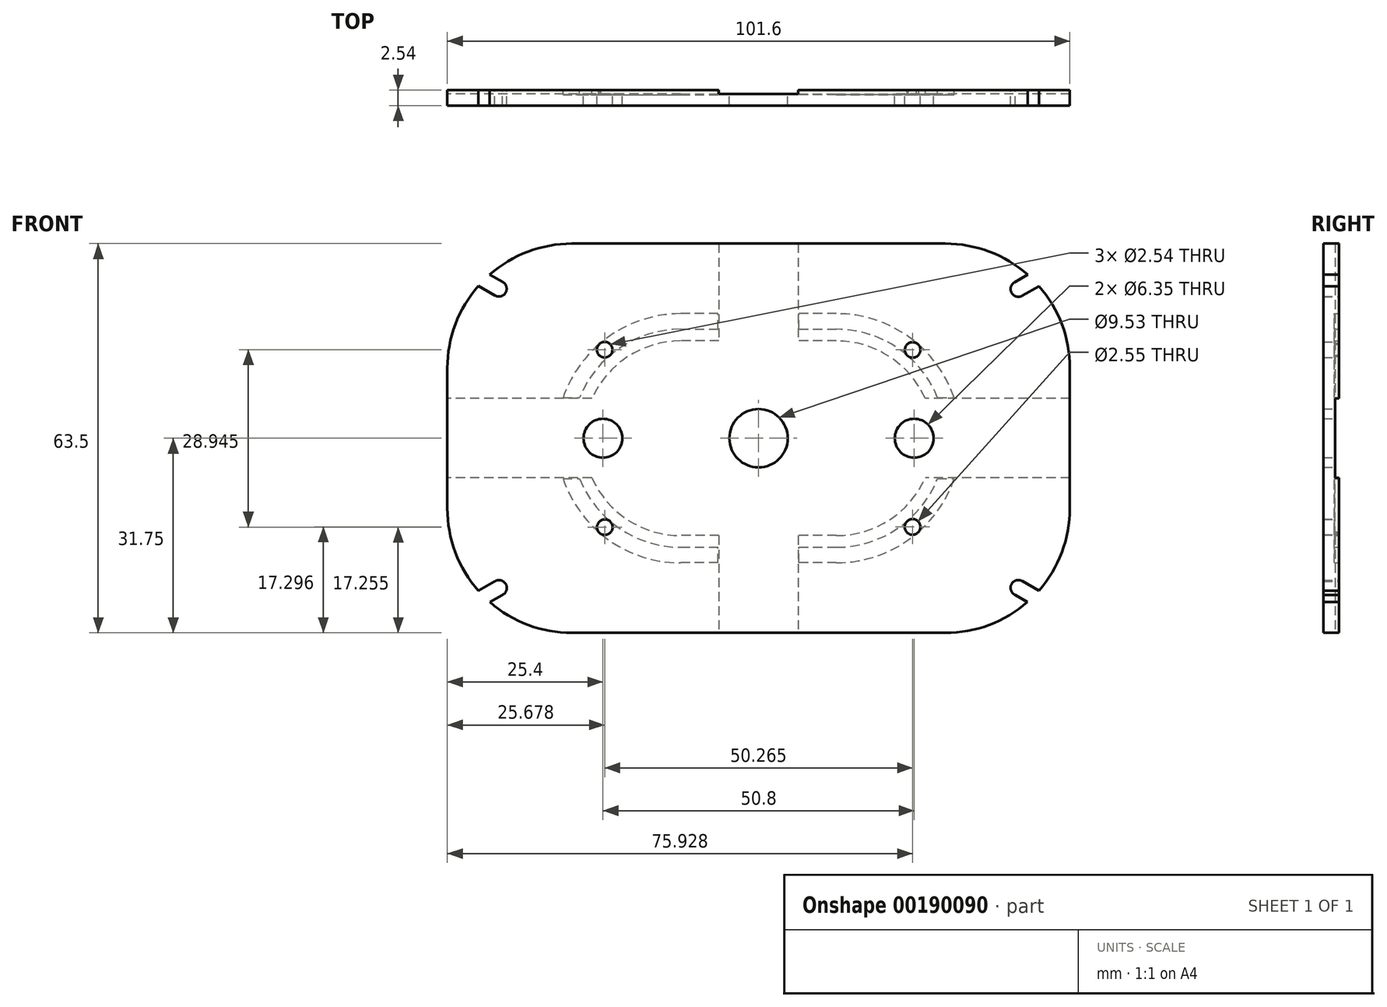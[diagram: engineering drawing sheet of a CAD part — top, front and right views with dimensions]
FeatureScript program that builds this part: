
annotation { "Feature Type Name" : "Feature", "Feature Type Description" : "" }
export const myFeature = defineFeature(function(context is Context, id is Id, definition is map)
    precondition{}
    {
        {
            var Q0;
            Q0=qCreatedBy(makeId("Front.planeOp"),FACE);
            var sketch = newSketch(context, id + "F0", { "sketchPlane" : qUnion([Q0])});
            skPoint(sketch, "E0.middle", {"position": v(0, 0) * mm});
            skLineSegment(sketch, "E1.bottom", {"start": v(-30.48, 31.75) * mm, "end": v(30.48, 31.75) * mm});
            skLineSegment(sketch, "E1.top", {"start": v(-30.48, -31.75) * mm, "end": v(30.48, -31.75) * mm});
            skLineSegment(sketch, "E1.left", {"start": v(-50.8, 11.43) * mm, "end": v(-50.8, -11.43) * mm});
            skLineSegment(sketch, "E1.right", {"start": v(50.8, 11.43) * mm, "end": v(50.8, -11.43) * mm});
            skPoint(sketch, "E2.visualSharp", {"position": v(-50.8, 31.75) * mm});
            skArc(sketch, "E2.filletArc", {"start": v(-30.48, 31.75) * mm, "mid": v(-44.85, 25.8) * mm, "end": v(-50.8, 11.43) * mm});
            skPoint(sketch, "E3.visualSharp", {"position": v(-50.8, -31.75) * mm});
            skArc(sketch, "E3.filletArc", {"start": v(-50.8, -11.43) * mm, "mid": v(-44.85, -25.8) * mm, "end": v(-30.48, -31.75) * mm});
            skPoint(sketch, "E4.visualSharp", {"position": v(50.8, -31.75) * mm});
            skArc(sketch, "E4.filletArc", {"start": v(30.48, -31.75) * mm, "mid": v(44.85, -25.8) * mm, "end": v(50.8, -11.43) * mm});
            skPoint(sketch, "E5.visualSharp", {"position": v(50.8, 31.75) * mm});
            skArc(sketch, "E5.filletArc", {"start": v(50.8, 11.43) * mm, "mid": v(44.85, 25.8) * mm, "end": v(30.48, 31.75) * mm});
            skSolve(sketch);
        }
        {
            var Q0;
            Q0 = qSketchRegion(id + "F0", true);
            extrude(context, id + "F1", {"entities" : qUnion([Q0]), "depth" : 2.54 * mm});
        }
        {
            var Q0;
            Q0=qCreatedBy(makeId("Front.planeOp"),FACE);
            var sketch = newSketch(context, id + "F2", { "sketchPlane" : qUnion([Q0])});
            skLineSegment(sketch, "E6.bottom", {"start": v(-12.7, 17.78) * mm, "end": v(12.7, 17.78) * mm});
            skLineSegment(sketch, "E6.top", {"start": v(-12.7, -17.78) * mm, "end": v(12.7, -17.78) * mm});
            skLineSegment(sketch, "E6.left", {"start": v(-30.48, 0) * mm, "end": v(-30.48, 0) * mm});
            skLineSegment(sketch, "E6.right", {"start": v(30.48, 0) * mm, "end": v(30.48, 0) * mm});
            skPoint(sketch, "E6.middle", {"position": v(0, 0) * mm});
            skPoint(sketch, "E7.visualSharp", {"position": v(-30.48, 17.78) * mm});
            skArc(sketch, "E7.filletArc", {"start": v(-12.7, 17.78) * mm, "mid": v(-25.27, 12.57) * mm, "end": v(-30.48, 0) * mm});
            skPoint(sketch, "E8.visualSharp", {"position": v(-30.48, -17.78) * mm});
            skArc(sketch, "E8.filletArc", {"start": v(-30.48, 0) * mm, "mid": v(-25.27, -12.57) * mm, "end": v(-12.7, -17.78) * mm});
            skPoint(sketch, "E9.visualSharp", {"position": v(30.48, 17.78) * mm});
            skArc(sketch, "E9.filletArc", {"start": v(30.48, 0) * mm, "mid": v(25.27, 12.57) * mm, "end": v(12.7, 17.78) * mm});
            skPoint(sketch, "E10.visualSharp", {"position": v(30.48, -17.78) * mm});
            skArc(sketch, "E10.filletArc", {"start": v(12.7, -17.78) * mm, "mid": v(25.27, -12.57) * mm, "end": v(30.48, 0) * mm});
            skLineSegment(sketch, "E11.bottom", {"start": v(12.7, 20.32) * mm, "end": v(-12.7, 20.32) * mm});
            skLineSegment(sketch, "E11.top", {"start": v(12.7, -20.32) * mm, "end": v(-12.7, -20.32) * mm});
            skLineSegment(sketch, "E11.left", {"start": v(33.02, 0) * mm, "end": v(33.02, 0) * mm});
            skLineSegment(sketch, "E11.right", {"start": v(-33.02, 0) * mm, "end": v(-33.02, 0) * mm});
            skPoint(sketch, "E12.visualSharp", {"position": v(-33.02, 20.32) * mm});
            skArc(sketch, "E12.filletArc", {"start": v(-12.7, 20.32) * mm, "mid": v(-27.07, 14.37) * mm, "end": v(-33.02, 0) * mm});
            skPoint(sketch, "E13.visualSharp", {"position": v(-33.02, -20.32) * mm});
            skArc(sketch, "E13.filletArc", {"start": v(-33.02, 0) * mm, "mid": v(-27.07, -14.37) * mm, "end": v(-12.7, -20.32) * mm});
            skPoint(sketch, "E14.visualSharp", {"position": v(33.02, -20.32) * mm});
            skArc(sketch, "E14.filletArc", {"start": v(12.7, -20.32) * mm, "mid": v(27.07, -14.37) * mm, "end": v(33.02, 0) * mm});
            skPoint(sketch, "E15.visualSharp", {"position": v(33.02, 20.32) * mm});
            skArc(sketch, "E15.filletArc", {"start": v(33.02, 0) * mm, "mid": v(27.07, 14.37) * mm, "end": v(12.7, 20.32) * mm});
            skSolve(sketch);
        }
        {
            var Q0;
            Q0 = qSketchRegion(id + "F2", true);
            extrude(context, id + "F3", {"entities" : qUnion([Q0]), "operationType" : NewBodyOperationType.ADD, "oppositeDirection" : true, "depth" : 12.7 * mm});
        }
        {
            var Q0;
            Q0=makeQuery(id+"F3.opExtrude","SWEPT_FACE",FACE,{"disambiguationData":[OSD([sQuery(id+"F2.wireOp",EDGE,"E11.bottom")])]});
            var sketch = newSketch(context, id + "F4", { "sketchPlane" : qUnion([Q0])});
            skLineSegment(sketch, "E16", {"start": v(0, 12.7) * mm, "end": v(-6.6, 12.7) * mm});
            skLineSegment(sketch, "E17", {"start": v(-6.6, 12.7) * mm, "end": v(-6.6, 0) * mm});
            skLineSegment(sketch, "E18", {"start": v(-6.6, 0) * mm, "end": v(6.6, 0) * mm});
            skLineSegment(sketch, "E19", {"start": v(6.6, 0) * mm, "end": v(6.6, 12.7) * mm});
            skLineSegment(sketch, "E20", {"start": v(6.6, 12.7) * mm, "end": v(0, 12.7) * mm});
            skSolve(sketch);
        }
        {
            var Q0;
            Q0 = qSketchRegion(id + "F4", true);
            extrude(context, id + "F5", {"entities" : qUnion([Q0]), "operationType" : NewBodyOperationType.REMOVE, "endBound" : BoundingType.THROUGH_ALL, "oppositeDirection" : true, "depth" : 25.4 * mm});
        }
        {
            var Q0;
            Q0=qCreatedBy(makeId("Right.planeOp"),FACE);
            var sketch = newSketch(context, id + "F6", { "sketchPlane" : qUnion([Q0])});
            skLineSegment(sketch, "E21", {"start": v(0, 0) * mm, "end": v(0, -6.6) * mm});
            skLineSegment(sketch, "E22", {"start": v(0, -6.6) * mm, "end": v(12.7, -6.6) * mm});
            skLineSegment(sketch, "E23", {"start": v(12.7, -6.6) * mm, "end": v(12.7, 6.6) * mm});
            skLineSegment(sketch, "E24", {"start": v(12.7, 6.6) * mm, "end": v(0, 6.6) * mm});
            skLineSegment(sketch, "E25", {"start": v(0, 6.6) * mm, "end": v(0, -6.6) * mm});
            skSolve(sketch);
        }
        {
            var Q0;
            Q0 = qSketchRegion(id + "F6", true);
            extrude(context, id + "F7", {"entities" : qUnion([Q0]), "operationType" : NewBodyOperationType.REMOVE, "endBound" : BoundingType.SYMMETRIC, "oppositeDirection" : true, "depth" : 152.4 * mm});
        }
        {
            var Q0;
            {var subQ0=sQuery(id+"F0.wireOp",EDGE,"E5.filletArc");var subQ1=sQuery(id+"F0.wireOp",EDGE,"E4.filletArc");var subQ2=sQuery(id+"F0.wireOp",EDGE,"E3.filletArc");var subQ3=sQuery(id+"F0.wireOp",EDGE,"E2.filletArc");var subQ4=sQuery(id+"F0.wireOp",EDGE,"E1.right");var subQ5=sQuery(id+"F0.wireOp",EDGE,"E1.left");var subQ6=sQuery(id+"F0.wireOp",EDGE,"E1.top");var subQ7=sQuery(id+"F0.wireOp",EDGE,"E1.bottom");var subQ8=makeQuery(id+"F1.opExtrude","CAP_FACE",FACE,{"disambiguationData":[OSD([subQ7,subQ6,subQ5,subQ4,subQ3,subQ2,subQ1,subQ0])],"isStart":true});Q0=makeQuery(id+"F7.boolean.opBoolean","MERGE",FACE,{"derivedFrom":[makeQuery(id+"F5.boolean.opBoolean","MERGE",FACE,{"derivedFrom":[makeQuery(id+"F3.boolean.opBoolean","SPLIT",FACE,{"disambiguationData":[TD([makeQuery(id+"F1.opExtrude","SWEPT_FACE",FACE,{"disambiguationData":[OSD([subQ7])]})])],"derivedFrom":subQ8}),makeQuery(id+"F3.boolean.opBoolean","SPLIT",FACE,{"disambiguationData":[TD([makeQuery(id+"F3.opExtrude","SWEPT_FACE",FACE,{"disambiguationData":[OSD([sQuery(id+"F2.wireOp",EDGE,"E6.bottom")])]})])],"derivedFrom":subQ8}),makeQuery(id+"F5.opExtrude","SWEPT_FACE",FACE,{"disambiguationData":[OSD([sQuery(id+"F4.wireOp",EDGE,"E18")])]})]}),makeQuery(id+"F7.opExtrude","SWEPT_FACE",FACE,{"disambiguationData":[OSD([sQuery(id+"F6.wireOp",EDGE,"E25")])]})]});}
            var sketch = newSketch(context, id + "F8", { "sketchPlane" : qUnion([Q0])});
            skPoint(sketch, "E26.middle", {"position": v(0, 0) * mm});
            skPoint(sketch, "E27.visualSharp", {"position": v(-27.94, -15.24) * mm});
            skPoint(sketch, "E28.visualSharp", {"position": v(-27.94, 15.24) * mm});
            skPoint(sketch, "E29.visualSharp", {"position": v(27.94, 15.24) * mm});
            skPoint(sketch, "E30.visualSharp", {"position": v(27.94, -15.24) * mm});
            skLineSegment(sketch, "E31.bottom", {"start": v(-12.7, 15.88) * mm, "end": v(12.7, 15.88) * mm});
            skLineSegment(sketch, "E31.top", {"start": v(-12.7, -15.88) * mm, "end": v(12.7, -15.88) * mm});
            skLineSegment(sketch, "E31.left", {"start": v(-28.58, 0) * mm, "end": v(-28.58, 0) * mm});
            skLineSegment(sketch, "E31.right", {"start": v(28.58, 0) * mm, "end": v(28.58, 0) * mm});
            skPoint(sketch, "E32.visualSharp", {"position": v(-28.58, -15.88) * mm});
            skArc(sketch, "E32.filletArc", {"start": v(-28.58, 0) * mm, "mid": v(-23.93, -11.23) * mm, "end": v(-12.7, -15.88) * mm});
            skPoint(sketch, "E33.visualSharp", {"position": v(-28.57, 15.88) * mm});
            skArc(sketch, "E33.filletArc", {"start": v(-12.7, 15.88) * mm, "mid": v(-23.93, 11.23) * mm, "end": v(-28.58, 0) * mm});
            skPoint(sketch, "E34.visualSharp", {"position": v(28.58, 15.88) * mm});
            skArc(sketch, "E34.filletArc", {"start": v(28.58, 0) * mm, "mid": v(23.93, 11.23) * mm, "end": v(12.7, 15.88) * mm});
            skPoint(sketch, "E35.visualSharp", {"position": v(28.57, -15.88) * mm});
            skArc(sketch, "E35.filletArc", {"start": v(12.7, -15.88) * mm, "mid": v(23.93, -11.23) * mm, "end": v(28.58, 0) * mm});
            skSolve(sketch);
        }
        {
            var Q0;
            Q0 = qSketchRegion(id + "F8", true);
            extrude(context, id + "F9", {"entities" : qUnion([Q0]), "operationType" : NewBodyOperationType.REMOVE, "oppositeDirection" : true, "depth" : 25.4 * mm});
        }
        {
            var Q0;
            {var subQ0=sQuery(id+"F0.wireOp",EDGE,"E5.filletArc");var subQ1=sQuery(id+"F0.wireOp",EDGE,"E4.filletArc");var subQ2=sQuery(id+"F0.wireOp",EDGE,"E3.filletArc");var subQ3=sQuery(id+"F0.wireOp",EDGE,"E2.filletArc");var subQ4=sQuery(id+"F0.wireOp",EDGE,"E1.right");var subQ5=sQuery(id+"F0.wireOp",EDGE,"E1.left");var subQ6=sQuery(id+"F0.wireOp",EDGE,"E1.top");var subQ7=sQuery(id+"F0.wireOp",EDGE,"E1.bottom");var subQ8=makeQuery(id+"F1.opExtrude","CAP_FACE",FACE,{"disambiguationData":[OSD([subQ7,subQ6,subQ5,subQ4,subQ3,subQ2,subQ1,subQ0])],"isStart":true});Q0=makeQuery(id+"F7.boolean.opBoolean","MERGE",FACE,{"derivedFrom":[makeQuery(id+"F5.boolean.opBoolean","MERGE",FACE,{"derivedFrom":[makeQuery(id+"F3.boolean.opBoolean","SPLIT",FACE,{"disambiguationData":[TD([makeQuery(id+"F1.opExtrude","SWEPT_FACE",FACE,{"disambiguationData":[OSD([subQ7])]})])],"derivedFrom":subQ8}),makeQuery(id+"F3.boolean.opBoolean","SPLIT",FACE,{"disambiguationData":[TD([makeQuery(id+"F3.opExtrude","SWEPT_FACE",FACE,{"disambiguationData":[OSD([sQuery(id+"F2.wireOp",EDGE,"E6.bottom")])]})])],"derivedFrom":subQ8}),makeQuery(id+"F5.opExtrude","SWEPT_FACE",FACE,{"disambiguationData":[OSD([sQuery(id+"F4.wireOp",EDGE,"E18")])]})]}),makeQuery(id+"F7.opExtrude","SWEPT_FACE",FACE,{"disambiguationData":[OSD([sQuery(id+"F6.wireOp",EDGE,"E25")])]})]});}
            var sketch = newSketch(context, id + "F10", { "sketchPlane" : qUnion([Q0])});
            skLineSegment(sketch, "E36.bottom", {"start": v(-57.15, 6.48) * mm, "end": v(57.15, 6.48) * mm});
            skLineSegment(sketch, "E36.top", {"start": v(-57.15, -6.48) * mm, "end": v(57.15, -6.48) * mm});
            skLineSegment(sketch, "E36.left", {"start": v(-57.15, 6.48) * mm, "end": v(-57.15, -6.48) * mm});
            skLineSegment(sketch, "E36.right", {"start": v(57.15, 6.48) * mm, "end": v(57.15, -6.48) * mm});
            skPoint(sketch, "E36.middle", {"position": v(0, 0) * mm});
            skLineSegment(sketch, "E37.bottom", {"start": v(-6.48, 44.45) * mm, "end": v(6.48, 44.45) * mm});
            skLineSegment(sketch, "E37.top", {"start": v(-6.48, -44.45) * mm, "end": v(6.48, -44.45) * mm});
            skLineSegment(sketch, "E37.left", {"start": v(-6.48, 44.45) * mm, "end": v(-6.48, -44.45) * mm});
            skLineSegment(sketch, "E37.right", {"start": v(6.48, 44.45) * mm, "end": v(6.48, -44.45) * mm});
            skSolve(sketch);
        }
        {
            var Q0;
            Q0 = qSketchRegion(id + "F10", true);
            extrude(context, id + "F11", {"entities" : qUnion([Q0]), "operationType" : NewBodyOperationType.REMOVE, "oppositeDirection" : true, "depth" : 0.64 * mm});
        }
        {
            var Q0;
            {var subQ0=sQuery(id+"F2.wireOp",EDGE,"E11.top");var subQ2=sQuery(id+"F2.wireOp",EDGE,"E10.filletArc");var subQ3=sQuery(id+"F2.wireOp",EDGE,"E9.filletArc");var subQ5=sQuery(id+"F2.wireOp",EDGE,"E15.filletArc");var subQ6=sQuery(id+"F2.wireOp",EDGE,"E14.filletArc");var subQ8=sQuery(id+"F2.wireOp",EDGE,"E6.top");var subQ9=makeQuery(id+"F3.opExtrude","SWEPT_FACE",FACE,{"disambiguationData":[OSD([subQ8])]});var subQ10=sQuery(id+"F2.wireOp",EDGE,"E11.bottom");var subQ11=sQuery(id+"F2.wireOp",EDGE,"E6.bottom");var subQ12=makeQuery(id+"F3.opExtrude","CAP_FACE",FACE,{"disambiguationData":[OSD([subQ11,subQ8,sQuery(id+"F2.wireOp",EDGE,"E7.filletArc"),sQuery(id+"F2.wireOp",EDGE,"E8.filletArc"),subQ3,subQ2,subQ10,subQ0,sQuery(id+"F2.wireOp",EDGE,"E12.filletArc"),sQuery(id+"F2.wireOp",EDGE,"E13.filletArc"),subQ6,subQ5])],"isStart":false});var subQ13=makeQuery(id+"F5.opExtrude","SWEPT_FACE",FACE,{"disambiguationData":[OSD([sQuery(id+"F4.wireOp",EDGE,"E19")])]});Q0=makeQuery(id+"F7.boolean.opBoolean","SPLIT",FACE,{"disambiguationData":[TD([subQ9])],"derivedFrom":makeQuery(id+"F5.boolean.opBoolean","SPLIT",FACE,{"disambiguationData":[TD([subQ13])],"derivedFrom":subQ12})});}
            var Q1;
            {var subQ0=sQuery(id+"F2.wireOp",EDGE,"E11.bottom");var subQ2=sQuery(id+"F2.wireOp",EDGE,"E10.filletArc");var subQ3=sQuery(id+"F2.wireOp",EDGE,"E9.filletArc");var subQ5=sQuery(id+"F2.wireOp",EDGE,"E15.filletArc");var subQ6=sQuery(id+"F2.wireOp",EDGE,"E14.filletArc");var subQ8=sQuery(id+"F2.wireOp",EDGE,"E6.bottom");var subQ9=makeQuery(id+"F3.opExtrude","SWEPT_FACE",FACE,{"disambiguationData":[OSD([subQ8])]});var subQ10=sQuery(id+"F2.wireOp",EDGE,"E11.top");var subQ11=sQuery(id+"F2.wireOp",EDGE,"E6.top");var subQ12=makeQuery(id+"F3.opExtrude","CAP_FACE",FACE,{"disambiguationData":[OSD([subQ8,subQ11,sQuery(id+"F2.wireOp",EDGE,"E7.filletArc"),sQuery(id+"F2.wireOp",EDGE,"E8.filletArc"),subQ3,subQ2,subQ0,subQ10,sQuery(id+"F2.wireOp",EDGE,"E12.filletArc"),sQuery(id+"F2.wireOp",EDGE,"E13.filletArc"),subQ6,subQ5])],"isStart":false});var subQ13=makeQuery(id+"F5.opExtrude","SWEPT_FACE",FACE,{"disambiguationData":[OSD([sQuery(id+"F4.wireOp",EDGE,"E19")])]});Q1=makeQuery(id+"F7.boolean.opBoolean","SPLIT",FACE,{"disambiguationData":[TD([subQ9])],"derivedFrom":makeQuery(id+"F5.boolean.opBoolean","SPLIT",FACE,{"disambiguationData":[TD([subQ13])],"derivedFrom":subQ12})});}
            var Q2;
            {var subQ0=sQuery(id+"F2.wireOp",EDGE,"E11.top");var subQ2=sQuery(id+"F2.wireOp",EDGE,"E13.filletArc");var subQ3=sQuery(id+"F2.wireOp",EDGE,"E12.filletArc");var subQ5=sQuery(id+"F2.wireOp",EDGE,"E8.filletArc");var subQ6=sQuery(id+"F2.wireOp",EDGE,"E7.filletArc");var subQ8=sQuery(id+"F2.wireOp",EDGE,"E6.top");var subQ9=makeQuery(id+"F3.opExtrude","SWEPT_FACE",FACE,{"disambiguationData":[OSD([subQ8])]});var subQ10=sQuery(id+"F2.wireOp",EDGE,"E11.bottom");var subQ11=sQuery(id+"F2.wireOp",EDGE,"E6.bottom");var subQ12=makeQuery(id+"F3.opExtrude","CAP_FACE",FACE,{"disambiguationData":[OSD([subQ11,subQ8,subQ6,subQ5,sQuery(id+"F2.wireOp",EDGE,"E9.filletArc"),sQuery(id+"F2.wireOp",EDGE,"E10.filletArc"),subQ10,subQ0,subQ3,subQ2,sQuery(id+"F2.wireOp",EDGE,"E14.filletArc"),sQuery(id+"F2.wireOp",EDGE,"E15.filletArc")])],"isStart":false});var subQ13=makeQuery(id+"F5.opExtrude","SWEPT_FACE",FACE,{"disambiguationData":[OSD([sQuery(id+"F4.wireOp",EDGE,"E17")])]});Q2=makeQuery(id+"F7.boolean.opBoolean","SPLIT",FACE,{"disambiguationData":[TD([subQ9])],"derivedFrom":makeQuery(id+"F5.boolean.opBoolean","SPLIT",FACE,{"disambiguationData":[TD([subQ13])],"derivedFrom":subQ12})});}
            var Q3;
            {var subQ0=sQuery(id+"F2.wireOp",EDGE,"E11.bottom");var subQ2=sQuery(id+"F2.wireOp",EDGE,"E8.filletArc");var subQ3=sQuery(id+"F2.wireOp",EDGE,"E7.filletArc");var subQ5=sQuery(id+"F2.wireOp",EDGE,"E13.filletArc");var subQ6=sQuery(id+"F2.wireOp",EDGE,"E12.filletArc");var subQ8=sQuery(id+"F2.wireOp",EDGE,"E6.bottom");var subQ9=makeQuery(id+"F3.opExtrude","SWEPT_FACE",FACE,{"disambiguationData":[OSD([subQ8])]});var subQ10=sQuery(id+"F2.wireOp",EDGE,"E11.top");var subQ11=sQuery(id+"F2.wireOp",EDGE,"E6.top");var subQ12=makeQuery(id+"F3.opExtrude","CAP_FACE",FACE,{"disambiguationData":[OSD([subQ8,subQ11,subQ3,subQ2,sQuery(id+"F2.wireOp",EDGE,"E9.filletArc"),sQuery(id+"F2.wireOp",EDGE,"E10.filletArc"),subQ0,subQ10,subQ6,subQ5,sQuery(id+"F2.wireOp",EDGE,"E14.filletArc"),sQuery(id+"F2.wireOp",EDGE,"E15.filletArc")])],"isStart":false});var subQ13=makeQuery(id+"F5.opExtrude","SWEPT_FACE",FACE,{"disambiguationData":[OSD([sQuery(id+"F4.wireOp",EDGE,"E17")])]});Q3=makeQuery(id+"F7.boolean.opBoolean","SPLIT",FACE,{"disambiguationData":[TD([subQ9])],"derivedFrom":makeQuery(id+"F5.boolean.opBoolean","SPLIT",FACE,{"disambiguationData":[TD([subQ13])],"derivedFrom":subQ12})});}
            extrude(context, id + "F12", {"entities" : qUnion([Q0, Q1, Q2, Q3]), "operationType" : NewBodyOperationType.REMOVE, "oppositeDirection" : true, "depth" : 13.46 * mm});
        }
        {
            var Q0;
            Q0=makeQuery(id+"F1.opExtrude","CAP_FACE",FACE,{"disambiguationData":[OSD([sQuery(id+"F0.wireOp",EDGE,"E1.bottom"),sQuery(id+"F0.wireOp",EDGE,"E1.top"),sQuery(id+"F0.wireOp",EDGE,"E1.left"),sQuery(id+"F0.wireOp",EDGE,"E1.right"),sQuery(id+"F0.wireOp",EDGE,"E2.filletArc"),sQuery(id+"F0.wireOp",EDGE,"E3.filletArc"),sQuery(id+"F0.wireOp",EDGE,"E4.filletArc"),sQuery(id+"F0.wireOp",EDGE,"E5.filletArc")])],"isStart":false});
            var sketch = newSketch(context, id + "F13", { "sketchPlane" : qUnion([Q0])});
            skLineSegment(sketch, "E38.bottom", {"start": v(12.7, -15.88) * mm, "end": v(-12.7, -15.88) * mm});
            skLineSegment(sketch, "E38.top", {"start": v(12.7, 15.88) * mm, "end": v(-12.7, 15.88) * mm});
            skLineSegment(sketch, "E38.left", {"start": v(28.58, 0) * mm, "end": v(28.58, 0) * mm});
            skLineSegment(sketch, "E38.right", {"start": v(-28.58, 0) * mm, "end": v(-28.58, 0) * mm});
            skPoint(sketch, "E38.middle", {"position": v(0, 0) * mm});
            skPoint(sketch, "E39.visualSharp", {"position": v(28.58, 15.88) * mm});
            skArc(sketch, "E39.filletArc", {"start": v(28.57, 0) * mm, "mid": v(23.93, 11.23) * mm, "end": v(12.7, 15.88) * mm});
            skPoint(sketch, "E40.visualSharp", {"position": v(28.58, -15.87) * mm});
            skArc(sketch, "E40.filletArc", {"start": v(12.7, -15.87) * mm, "mid": v(23.93, -11.23) * mm, "end": v(28.58, 0) * mm});
            skPoint(sketch, "E41.visualSharp", {"position": v(-28.58, -15.88) * mm});
            skArc(sketch, "E41.filletArc", {"start": v(-28.57, 0) * mm, "mid": v(-23.93, -11.23) * mm, "end": v(-12.7, -15.88) * mm});
            skPoint(sketch, "E42.visualSharp", {"position": v(-28.58, 15.87) * mm});
            skArc(sketch, "E42.filletArc", {"start": v(-12.7, 15.88) * mm, "mid": v(-23.93, 11.23) * mm, "end": v(-28.58, 0) * mm});
            skSolve(sketch);
        }
        {
            var Q0;
            Q0 = qSketchRegion(id + "F13", true);
            extrude(context, id + "F14", {"entities" : qUnion([Q0]), "operationType" : NewBodyOperationType.ADD, "oppositeDirection" : true, "depth" : 1.9 * mm});
        }
        {
            var Q0;
            {var subQ0=sQuery(id+"F0.wireOp",EDGE,"E1.top");var subQ2=sQuery(id+"F10.wireOp",EDGE,"E37.left");var subQ3=sQuery(id+"F10.wireOp",EDGE,"E37.top");var subQ8=sQuery(id+"F10.wireOp",EDGE,"E36.top");var subQ10=sQuery(id+"F10.wireOp",EDGE,"E37.right");var subQ14=sQuery(id+"F10.wireOp",EDGE,"E37.bottom");var subQ15=sQuery(id+"F10.wireOp",EDGE,"E36.right");var subQ16=sQuery(id+"F10.wireOp",EDGE,"E36.left");var subQ17=sQuery(id+"F10.wireOp",EDGE,"E36.bottom");var subQ18=makeQuery(id+"F11.opExtrude","CAP_FACE",FACE,{"disambiguationData":[OSD([subQ17,subQ8,subQ16,subQ15,subQ14,subQ3,subQ2,subQ10])],"isStart":false});var subQ19=sQuery(id+"F0.wireOp",EDGE,"E1.bottom");var subQ29=sQuery(id+"F0.wireOp",EDGE,"E1.left");var subQ38=sQuery(id+"F0.wireOp",EDGE,"E1.right");Q0=makeQuery(id+"F14.boolean.opBoolean","MERGE",FACE,{"derivedFrom":[makeQuery(id+"F11.boolean.opBoolean","COPY",FACE,{"disambiguationData":[TD([makeQuery(id+"F1.opExtrude","SWEPT_FACE",FACE,{"disambiguationData":[OSD([subQ38])]})])],"derivedFrom":subQ18}),makeQuery(id+"F11.boolean.opBoolean","COPY",FACE,{"disambiguationData":[TD([makeQuery(id+"F1.opExtrude","SWEPT_FACE",FACE,{"disambiguationData":[OSD([subQ29])]})])],"derivedFrom":subQ18}),makeQuery(id+"F11.boolean.opBoolean","COPY",FACE,{"disambiguationData":[TD([makeQuery(id+"F1.opExtrude","SWEPT_FACE",FACE,{"disambiguationData":[OSD([subQ19])]})])],"derivedFrom":subQ18}),makeQuery(id+"F11.boolean.opBoolean","COPY",FACE,{"disambiguationData":[TD([makeQuery(id+"F1.opExtrude","SWEPT_FACE",FACE,{"disambiguationData":[OSD([subQ0])]})])],"derivedFrom":subQ18}),makeQuery(id+"F14.opExtrude","CAP_FACE",FACE,{"disambiguationData":[OSD([sQuery(id+"F13.wireOp",EDGE,"E38.bottom"),sQuery(id+"F13.wireOp",EDGE,"E38.top"),sQuery(id+"F13.wireOp",EDGE,"E39.filletArc"),sQuery(id+"F13.wireOp",EDGE,"E40.filletArc"),sQuery(id+"F13.wireOp",EDGE,"E41.filletArc"),sQuery(id+"F13.wireOp",EDGE,"E42.filletArc")])],"isStart":false})]});}
            var sketch = newSketch(context, id + "F15", { "sketchPlane" : qUnion([Q0])});
            skCircle(sketch, "E43", {"center": v(0, 0) * mm, "radius": 4.76 * mm});
            skCircle(sketch, "E44", {"center": v(-25.4, 0) * mm, "radius": 3.18 * mm});
            skCircle(sketch, "E45", {"center": v(25.4, 0) * mm, "radius": 3.18 * mm});
            skSolve(sketch);
        }
        {
            var Q0;
            Q0 = qSketchRegion(id + "F15", true);
            extrude(context, id + "F16", {"entities" : qUnion([Q0]), "operationType" : NewBodyOperationType.REMOVE, "oppositeDirection" : true, "depth" : 25.4 * mm});
        }
        {
            var Q0;
            {var subQ3=sQuery(id+"F0.wireOp",EDGE,"E5.filletArc");var subQ4=sQuery(id+"F0.wireOp",EDGE,"E4.filletArc");var subQ5=sQuery(id+"F0.wireOp",EDGE,"E3.filletArc");var subQ6=sQuery(id+"F0.wireOp",EDGE,"E2.filletArc");var subQ7=sQuery(id+"F0.wireOp",EDGE,"E1.right");var subQ8=sQuery(id+"F0.wireOp",EDGE,"E1.left");var subQ9=sQuery(id+"F0.wireOp",EDGE,"E1.top");var subQ10=sQuery(id+"F0.wireOp",EDGE,"E1.bottom");var subQ11=makeQuery(id+"F1.opExtrude","CAP_FACE",FACE,{"disambiguationData":[OSD([subQ10,subQ9,subQ8,subQ7,subQ6,subQ5,subQ4,subQ3])],"isStart":true});var subQ12=makeQuery(id+"F7.opExtrude","SWEPT_FACE",FACE,{"disambiguationData":[OSD([sQuery(id+"F6.wireOp",EDGE,"E25")])]});var subQ23=sQuery(id+"F2.wireOp",EDGE,"E6.bottom");var subQ25=makeQuery(id+"F5.opExtrude","SWEPT_FACE",FACE,{"disambiguationData":[OSD([sQuery(id+"F4.wireOp",EDGE,"E18")])]});var subQ30=makeQuery(id+"F1.opExtrude","SWEPT_FACE",FACE,{"disambiguationData":[OSD([subQ4])]});Q0=makeQuery(id+"F11.boolean.opBoolean","SPLIT",FACE,{"disambiguationData":[TD([subQ30])],"derivedFrom":makeQuery(id+"F7.boolean.opBoolean","MERGE",FACE,{"derivedFrom":[makeQuery(id+"F5.boolean.opBoolean","MERGE",FACE,{"derivedFrom":[makeQuery(id+"F3.boolean.opBoolean","SPLIT",FACE,{"disambiguationData":[TD([makeQuery(id+"F1.opExtrude","SWEPT_FACE",FACE,{"disambiguationData":[OSD([subQ10])]})])],"derivedFrom":subQ11}),makeQuery(id+"F3.boolean.opBoolean","SPLIT",FACE,{"disambiguationData":[TD([makeQuery(id+"F3.opExtrude","SWEPT_FACE",FACE,{"disambiguationData":[OSD([subQ23])]})])],"derivedFrom":subQ11}),subQ25]}),subQ12]})});}
            var sketch = newSketch(context, id + "F17", { "sketchPlane" : qUnion([Q0])});
            skLineSegment(sketch, "E46", {"start": v(51.17, -29.5) * mm, "end": v(47.67, -27.48) * mm});
            skCircle(sketch, "E47", {"center": v(-25.13, -14.45) * mm, "radius": 1.28 * mm});
            skCircle(sketch, "E48", {"center": v(-25.14, 14.41) * mm, "radius": 1.27 * mm});
            skCircle(sketch, "E49", {"center": v(25.12, 14.45) * mm, "radius": 1.27 * mm});
            skCircle(sketch, "E50", {"center": v(25.1, -14.5) * mm, "radius": 1.27 * mm});
            skLineSegment(sketch, "E51", {"start": v(-43.03, -23.29) * mm, "end": v(-48.14, -26.22) * mm});
            skLineSegment(sketch, "E52", {"start": v(-48.14, -26.22) * mm, "end": v(-46.87, -28.43) * mm});
            skLineSegment(sketch, "E53", {"start": v(-46.87, -28.43) * mm, "end": v(-41.86, -25.55) * mm});
            skLineSegment(sketch, "E54", {"start": v(-41.86, -25.55) * mm, "end": v(-41.86, -25.54) * mm});
            skArc(sketch, "E55", {"start": v(-41.86, -25.54) * mm, "mid": v(-41.27, -23.8) * mm, "end": v(-43.03, -23.29) * mm});
            skLineSegment(sketch, "E56", {"start": v(-41.77, 25.44) * mm, "end": v(-42.2, 25.7) * mm});
            skLineSegment(sketch, "E57", {"start": v(-42.2, 25.7) * mm, "end": v(-46.04, 27.9) * mm});
            skLineSegment(sketch, "E58", {"start": v(-46.04, 27.9) * mm, "end": v(-47.3, 25.7) * mm});
            skLineSegment(sketch, "E59", {"start": v(-47.3, 25.7) * mm, "end": v(-43.05, 23.25) * mm});
            skArc(sketch, "E60", {"start": v(-43.05, 23.25) * mm, "mid": v(-41.3, 23.7) * mm, "end": v(-41.78, 25.45) * mm});
            skPoint(sketch, "E61.trimOffspring.end.orphan", {"position": v(-44.85, 29.43) * mm});
            skLineSegment(sketch, "E62", {"start": v(41.75, 25.48) * mm, "end": v(46.63, 28.29) * mm});
            skLineSegment(sketch, "E63", {"start": v(46.63, 28.29) * mm, "end": v(47.9, 26.08) * mm});
            skLineSegment(sketch, "E64", {"start": v(47.9, 26.08) * mm, "end": v(43.02, 23.28) * mm});
            skLineSegment(sketch, "E65", {"start": v(43.02, 23.28) * mm, "end": v(43.02, 23.28) * mm});
            skArc(sketch, "E66", {"start": v(41.75, 25.48) * mm, "mid": v(41.28, 23.74) * mm, "end": v(43.02, 23.28) * mm});
            skPoint(sketch, "E67.orphan", {"position": v(51.17, 29.43) * mm});
            skLineSegment(sketch, "E68", {"start": v(43, -23.32) * mm, "end": v(48.3, -26.37) * mm});
            skLineSegment(sketch, "E69", {"start": v(48.3, -26.37) * mm, "end": v(47.04, -28.57) * mm});
            skLineSegment(sketch, "E70", {"start": v(47.04, -28.57) * mm, "end": v(41.8, -25.56) * mm});
            skLineSegment(sketch, "E71", {"start": v(42.36, -24.43) * mm, "end": v(42.36, -24.42) * mm});
            skArc(sketch, "E72", {"start": v(43.46, -25.06) * mm, "mid": v(43.46, -25.06) * mm, "end": v(43.46, -25.05) * mm});
            skArc(sketch, "E73.trimOffspring", {"start": v(43.06, -23.35) * mm, "mid": v(41.26, -23.78) * mm, "end": v(41.8, -25.56) * mm});
            skLineSegment(sketch, "E74.trimOffspring", {"start": v(47.67, -27.48) * mm, "end": v(51.17, -29.5) * mm});
            skSolve(sketch);
        }
        {
            var Q0;
            Q0 = qSketchRegion(id + "F17", true);
            extrude(context, id + "F18", {"entities" : qUnion([Q0]), "operationType" : NewBodyOperationType.REMOVE, "oppositeDirection" : true, "depth" : 25.4 * mm});
        }
    });
